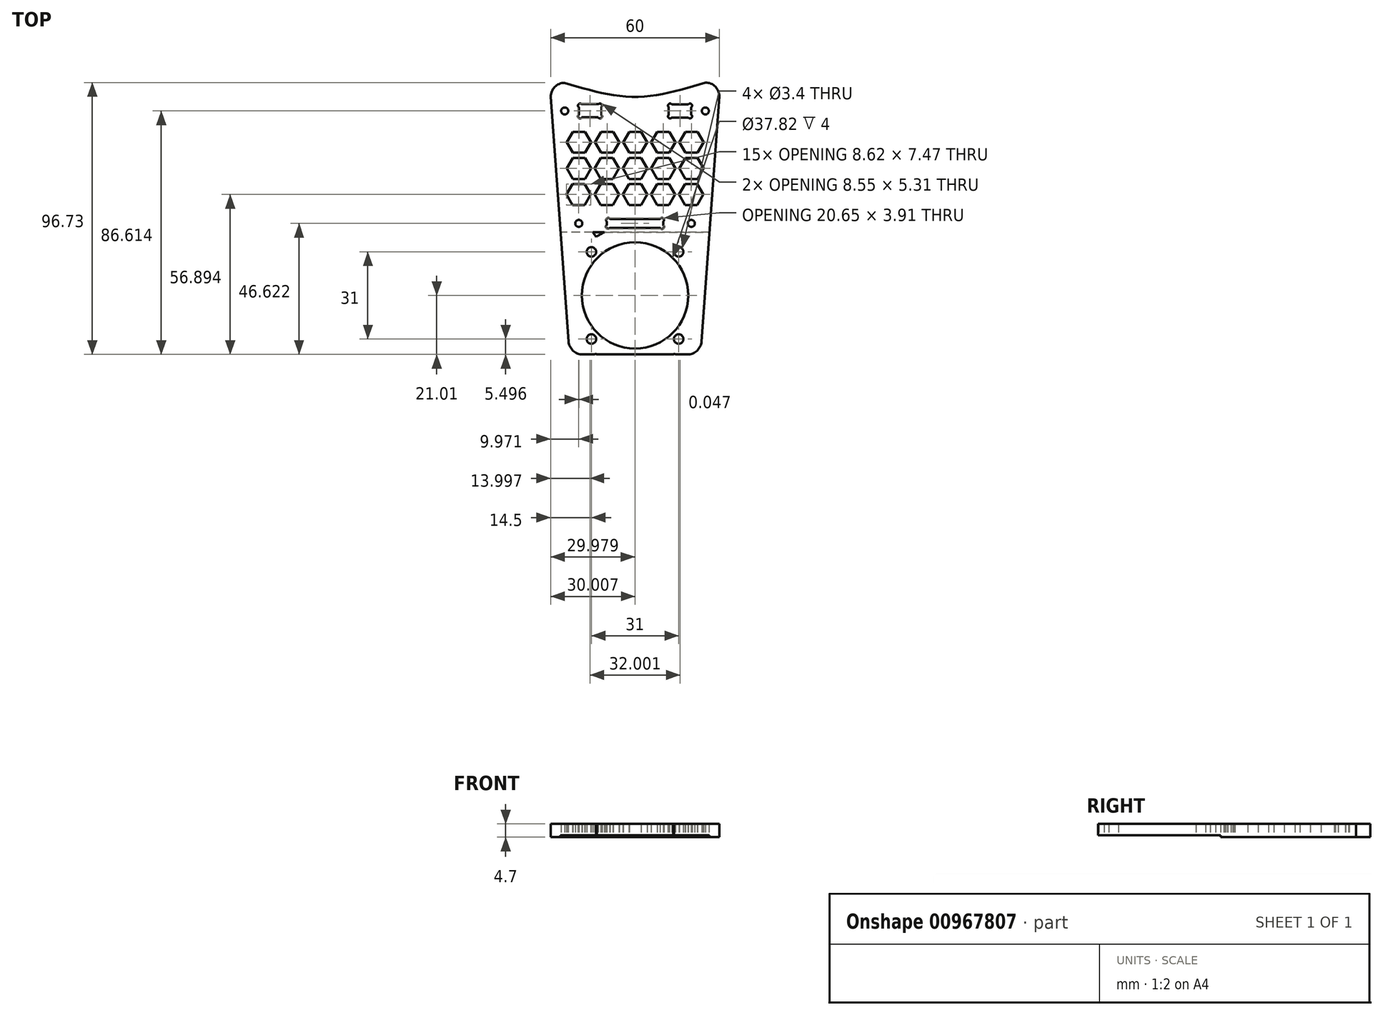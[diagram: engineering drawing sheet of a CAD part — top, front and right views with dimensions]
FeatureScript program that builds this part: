
annotation { "Feature Type Name" : "Feature", "Feature Type Description" : "" }
export const myFeature = defineFeature(function(context is Context, id is Id, definition is map)
    precondition{}
    {
        {
            var Q0;
            Q0=qCreatedBy(makeId("Top.planeOp"),FACE);
            var sketch = newSketch(context, id + "F0", { "sketchPlane" : qUnion([Q0])});
            skCircle(sketch, "E0", {"center": v(-24.72, 17.48) * mm, "radius": 1.25 * mm});
            skCircle(sketch, "E1", {"center": v(25.28, 17.48) * mm, "radius": 1.25 * mm});
            skLineSegment(sketch, "E2.bottom", {"start": v(20.28, 19.83) * mm, "end": v(12.28, 19.83) * mm});
            skLineSegment(sketch, "E2.top", {"start": v(20.28, 15.13) * mm, "end": v(12.28, 15.13) * mm});
            skLineSegment(sketch, "E2.left", {"start": v(20.28, 19.83) * mm, "end": v(20.28, 15.13) * mm});
            skLineSegment(sketch, "E2.right", {"start": v(12.28, 19.83) * mm, "end": v(12.28, 15.13) * mm});
            skPoint(sketch, "E3", {"position": v(0.28, -22.52) * mm});
            skLineSegment(sketch, "E4.bottom", {"start": v(-9.72, -20.9) * mm, "end": v(10.28, -20.9) * mm});
            skLineSegment(sketch, "E4.top", {"start": v(-9.72, -24.14) * mm, "end": v(10.28, -24.14) * mm});
            skLineSegment(sketch, "E4.left", {"start": v(-9.72, -20.9) * mm, "end": v(-9.72, -24.14) * mm});
            skLineSegment(sketch, "E4.right", {"start": v(10.28, -20.9) * mm, "end": v(10.28, -24.14) * mm});
            skCircle(sketch, "E5", {"center": v(20.28, -22.52) * mm, "radius": 1.25 * mm});
            skCircle(sketch, "E6", {"center": v(-19.72, -22.52) * mm, "radius": 1.25 * mm});
            skPoint(sketch, "E7.visualSharp", {"position": v(-29.72, 27.48) * mm});
            skArc(sketch, "E7.filletArc", {"start": v(-24.72, 27.48) * mm, "mid": v(-28.26, 26.02) * mm, "end": v(-29.72, 22.48) * mm});
            skPoint(sketch, "E8.visualSharp", {"position": v(30.28, 27.48) * mm});
            skArc(sketch, "E8.filletArc", {"start": v(30.28, 22.59) * mm, "mid": v(28.82, 26.12) * mm, "end": v(25.28, 27.59) * mm});
            skCircle(sketch, "E9", {"center": v(19.8, 15.57) * mm, "radius": 0.75 * mm});
            skCircle(sketch, "E10", {"center": v(12.75, 15.57) * mm, "radius": 0.75 * mm});
            skCircle(sketch, "E11", {"center": v(12.75, 19.38) * mm, "radius": 0.75 * mm});
            skCircle(sketch, "E12", {"center": v(19.8, 19.38) * mm, "radius": 0.75 * mm});
            skLineSegment(sketch, "E13.bottom", {"start": v(-11.72, 19.88) * mm, "end": v(-19.72, 19.88) * mm});
            skLineSegment(sketch, "E13.top", {"start": v(-11.72, 15.18) * mm, "end": v(-19.72, 15.18) * mm});
            skLineSegment(sketch, "E13.left", {"start": v(-11.72, 19.88) * mm, "end": v(-11.72, 15.18) * mm});
            skLineSegment(sketch, "E13.right", {"start": v(-19.72, 19.88) * mm, "end": v(-19.72, 15.18) * mm});
            skCircle(sketch, "E14", {"center": v(-12.2, 15.56) * mm, "radius": 0.75 * mm});
            skCircle(sketch, "E15", {"center": v(-19.25, 15.56) * mm, "radius": 0.75 * mm});
            skCircle(sketch, "E16", {"center": v(-19.25, 19.38) * mm, "radius": 0.75 * mm});
            skCircle(sketch, "E17", {"center": v(-12.2, 19.38) * mm, "radius": 0.75 * mm});
            skCircle(sketch, "E18", {"center": v(9.82, -21.3) * mm, "radius": 0.75 * mm});
            skCircle(sketch, "E19", {"center": v(-9.25, -21.33) * mm, "radius": 0.75 * mm});
            skCircle(sketch, "E20", {"center": v(-9.32, -23.66) * mm, "radius": 0.75 * mm});
            skCircle(sketch, "E21", {"center": v(9.83, -23.73) * mm, "radius": 0.75 * mm});
            skFitSpline(sketch, "E22", {"points": [v(-24.72, 27.48) * mm, v(0.28, 22.48) * mm, v(25.28, 27.59) * mm], "startDerivative": vector(50, -15) * mm, "endDerivative": vector(50, 15) * mm});
            skPoint(sketch, "E23", {"position": v(28, -0.27) * mm});
            skPoint(sketch, "E24.startSnap0", {"position": v(-15.72, 15.18) * mm});
            skPoint(sketch, "E25", {"position": v(-24.72, -45.86) * mm});
            skPoint(sketch, "E26", {"position": v(25.28, -45.72) * mm});
            skPoint(sketch, "E27.newPointB", {"position": v(25.28, -45.5) * mm});
            skPoint(sketch, "E28.newPointA", {"position": v(26.62, -27.41) * mm});
            skCircle(sketch, "E29.cCircle", {"center": v(20.25, -12.25) * mm, "radius": 3.73 * mm, "construction": true});
            skLineSegment(sketch, "E29.0", {"start": v(24.56, -12.25) * mm, "end": v(22.4, -15.98) * mm});
            skLineSegment(sketch, "E29.1", {"start": v(22.4, -15.98) * mm, "end": v(18.1, -15.98) * mm});
            skLineSegment(sketch, "E29.2", {"start": v(18.1, -15.98) * mm, "end": v(15.94, -12.25) * mm});
            skLineSegment(sketch, "E29.3", {"start": v(15.94, -12.25) * mm, "end": v(18.1, -8.51) * mm});
            skLineSegment(sketch, "E29.4", {"start": v(18.1, -8.51) * mm, "end": v(22.4, -8.51) * mm});
            skLineSegment(sketch, "E29.5", {"start": v(22.4, -8.51) * mm, "end": v(24.56, -12.25) * mm});
            skPoint(sketch, "E29.0.midPoint", {"position": v(23.48, -14.11) * mm});
            skLineSegment(sketch, "E30.1.0.0", {"start": v(12.4, -8.51) * mm, "end": v(14.56, -12.25) * mm});
            skCircle(sketch, "E30.1.0.1", {"center": v(10.25, -12.25) * mm, "radius": 3.73 * mm, "construction": true});
            skLineSegment(sketch, "E30.1.0.2", {"start": v(8.1, -15.98) * mm, "end": v(5.94, -12.25) * mm});
            skLineSegment(sketch, "E30.1.0.3", {"start": v(12.4, -15.98) * mm, "end": v(8.1, -15.98) * mm});
            skPoint(sketch, "E30.1.0.4", {"position": v(13.48, -14.11) * mm});
            skLineSegment(sketch, "E30.1.0.5", {"start": v(5.94, -12.25) * mm, "end": v(8.1, -8.51) * mm});
            skLineSegment(sketch, "E30.1.0.6", {"start": v(8.1, -8.51) * mm, "end": v(12.4, -8.51) * mm});
            skLineSegment(sketch, "E30.1.0.7", {"start": v(14.56, -12.25) * mm, "end": v(12.4, -15.98) * mm});
            skLineSegment(sketch, "E30.direction1", {"start": v(18.1, -15.98) * mm, "end": v(8.1, -15.98) * mm, "construction": true});
            skLineSegment(sketch, "E30.direction2", {"start": v(18.1, -15.98) * mm, "end": v(18.14, -6.68) * mm, "construction": true});
            skCircle(sketch, "E31", {"center": v(0.28, -48.14) * mm, "radius": 12 * mm});
            skLineSegment(sketch, "E32", {"start": v(-18.37, -69.14) * mm, "end": v(18.92, -69.14) * mm});
            skPoint(sketch, "E33.visualSharp", {"position": v(-23.01, -69.14) * mm});
            skArc(sketch, "E33.filletArc", {"start": v(-23.35, -64.5) * mm, "mid": v(-21.77, -67.8) * mm, "end": v(-18.37, -69.14) * mm});
            skPoint(sketch, "E34.visualSharp", {"position": v(23.56, -69.14) * mm});
            skArc(sketch, "E34.filletArc", {"start": v(18.92, -69.14) * mm, "mid": v(22.32, -67.8) * mm, "end": v(23.9, -64.5) * mm});
            skCircle(sketch, "E35", {"center": v(15.78, -32.64) * mm, "radius": 1.7 * mm});
            skCircle(sketch, "E36", {"center": v(-15.22, -32.64) * mm, "radius": 1.7 * mm});
            skCircle(sketch, "E37", {"center": v(-15.22, -63.64) * mm, "radius": 1.7 * mm});
            skCircle(sketch, "E38", {"center": v(15.78, -63.64) * mm, "radius": 1.7 * mm});
            skLineSegment(sketch, "E39.0.2.0", {"start": v(2.4, -8.51) * mm, "end": v(4.56, -12.25) * mm});
            skCircle(sketch, "E39.3.2.0", {"center": v(0.25, -12.25) * mm, "radius": 3.73 * mm, "construction": true});
            skLineSegment(sketch, "E39.5.2.0", {"start": v(-1.9, -15.98) * mm, "end": v(-4.06, -12.25) * mm});
            skLineSegment(sketch, "E39.8.2.0", {"start": v(2.4, -15.98) * mm, "end": v(-1.9, -15.98) * mm});
            skPoint(sketch, "E39.11.2.0", {"position": v(3.48, -14.11) * mm});
            skLineSegment(sketch, "E39.12.2.0", {"start": v(-4.06, -12.25) * mm, "end": v(-1.9, -8.51) * mm});
            skLineSegment(sketch, "E39.15.2.0", {"start": v(-1.9, -8.51) * mm, "end": v(2.4, -8.51) * mm});
            skLineSegment(sketch, "E39.18.2.0", {"start": v(4.56, -12.25) * mm, "end": v(2.4, -15.98) * mm});
            skLineSegment(sketch, "E39.0.3.0", {"start": v(-7.6, -8.51) * mm, "end": v(-5.44, -12.25) * mm});
            skCircle(sketch, "E39.3.3.0", {"center": v(-9.75, -12.25) * mm, "radius": 3.73 * mm, "construction": true});
            skLineSegment(sketch, "E39.5.3.0", {"start": v(-11.9, -15.98) * mm, "end": v(-14.06, -12.25) * mm});
            skLineSegment(sketch, "E39.8.3.0", {"start": v(-7.6, -15.98) * mm, "end": v(-11.9, -15.98) * mm});
            skPoint(sketch, "E39.11.3.0", {"position": v(-6.52, -14.11) * mm});
            skLineSegment(sketch, "E39.12.3.0", {"start": v(-14.06, -12.25) * mm, "end": v(-11.9, -8.51) * mm});
            skLineSegment(sketch, "E39.15.3.0", {"start": v(-11.9, -8.51) * mm, "end": v(-7.6, -8.51) * mm});
            skLineSegment(sketch, "E39.18.3.0", {"start": v(-5.44, -12.25) * mm, "end": v(-7.6, -15.98) * mm});
            skLineSegment(sketch, "E40.0.0.1", {"start": v(22.45, 0.78) * mm, "end": v(24.6, -2.95) * mm});
            skCircle(sketch, "E40.3.0.1", {"center": v(20.3, -2.95) * mm, "radius": 3.73 * mm, "construction": true});
            skLineSegment(sketch, "E40.5.0.1", {"start": v(18.14, -6.68) * mm, "end": v(15.99, -2.95) * mm});
            skLineSegment(sketch, "E40.8.0.1", {"start": v(22.45, -6.68) * mm, "end": v(18.14, -6.68) * mm});
            skPoint(sketch, "E40.11.0.1", {"position": v(23.53, -4.82) * mm});
            skLineSegment(sketch, "E40.12.0.1", {"start": v(15.99, -2.95) * mm, "end": v(18.14, 0.78) * mm});
            skLineSegment(sketch, "E40.15.0.1", {"start": v(18.14, 0.78) * mm, "end": v(22.45, 0.78) * mm});
            skLineSegment(sketch, "E40.18.0.1", {"start": v(24.6, -2.95) * mm, "end": v(22.45, -6.68) * mm});
            skLineSegment(sketch, "E40.0.0.2", {"start": v(22.5, 10.07) * mm, "end": v(24.66, 6.34) * mm});
            skCircle(sketch, "E40.3.0.2", {"center": v(20.34, 6.34) * mm, "radius": 3.73 * mm, "construction": true});
            skLineSegment(sketch, "E40.5.0.2", {"start": v(18.19, 2.6) * mm, "end": v(16.03, 6.34) * mm});
            skLineSegment(sketch, "E40.8.0.2", {"start": v(22.5, 2.6) * mm, "end": v(18.19, 2.6) * mm});
            skPoint(sketch, "E40.11.0.2", {"position": v(23.58, 4.48) * mm});
            skLineSegment(sketch, "E40.12.0.2", {"start": v(16.03, 6.34) * mm, "end": v(18.19, 10.07) * mm});
            skLineSegment(sketch, "E40.15.0.2", {"start": v(18.19, 10.07) * mm, "end": v(22.5, 10.07) * mm});
            skLineSegment(sketch, "E40.18.0.2", {"start": v(24.66, 6.34) * mm, "end": v(22.5, 2.6) * mm});
            skLineSegment(sketch, "E40.0.1.1", {"start": v(12.45, 0.78) * mm, "end": v(14.6, -2.95) * mm});
            skCircle(sketch, "E40.3.1.1", {"center": v(10.3, -2.95) * mm, "radius": 3.73 * mm, "construction": true});
            skLineSegment(sketch, "E40.5.1.1", {"start": v(8.14, -6.68) * mm, "end": v(5.99, -2.95) * mm});
            skLineSegment(sketch, "E40.8.1.1", {"start": v(12.45, -6.68) * mm, "end": v(8.14, -6.68) * mm});
            skPoint(sketch, "E40.11.1.1", {"position": v(13.53, -4.82) * mm});
            skLineSegment(sketch, "E40.12.1.1", {"start": v(5.99, -2.95) * mm, "end": v(8.14, 0.78) * mm});
            skLineSegment(sketch, "E40.15.1.1", {"start": v(8.14, 0.78) * mm, "end": v(12.45, 0.78) * mm});
            skLineSegment(sketch, "E40.18.1.1", {"start": v(14.6, -2.95) * mm, "end": v(12.45, -6.68) * mm});
            skLineSegment(sketch, "E40.0.1.2", {"start": v(12.5, 10.07) * mm, "end": v(14.66, 6.34) * mm});
            skCircle(sketch, "E40.3.1.2", {"center": v(10.34, 6.34) * mm, "radius": 3.73 * mm, "construction": true});
            skLineSegment(sketch, "E40.5.1.2", {"start": v(8.19, 2.6) * mm, "end": v(6.03, 6.34) * mm});
            skLineSegment(sketch, "E40.8.1.2", {"start": v(12.5, 2.6) * mm, "end": v(8.19, 2.6) * mm});
            skPoint(sketch, "E40.11.1.2", {"position": v(13.58, 4.48) * mm});
            skLineSegment(sketch, "E40.12.1.2", {"start": v(6.03, 6.34) * mm, "end": v(8.19, 10.07) * mm});
            skLineSegment(sketch, "E40.15.1.2", {"start": v(8.19, 10.07) * mm, "end": v(12.5, 10.07) * mm});
            skLineSegment(sketch, "E40.18.1.2", {"start": v(14.66, 6.34) * mm, "end": v(12.5, 2.6) * mm});
            skLineSegment(sketch, "E40.0.2.1", {"start": v(2.45, 0.78) * mm, "end": v(4.6, -2.95) * mm});
            skCircle(sketch, "E40.3.2.1", {"center": v(0.3, -2.95) * mm, "radius": 3.73 * mm, "construction": true});
            skLineSegment(sketch, "E40.5.2.1", {"start": v(-1.86, -6.68) * mm, "end": v(-4.01, -2.95) * mm});
            skLineSegment(sketch, "E40.8.2.1", {"start": v(2.45, -6.68) * mm, "end": v(-1.86, -6.68) * mm});
            skPoint(sketch, "E40.11.2.1", {"position": v(3.53, -4.82) * mm});
            skLineSegment(sketch, "E40.12.2.1", {"start": v(-4.01, -2.95) * mm, "end": v(-1.86, 0.78) * mm});
            skLineSegment(sketch, "E40.15.2.1", {"start": v(-1.86, 0.78) * mm, "end": v(2.45, 0.78) * mm});
            skLineSegment(sketch, "E40.18.2.1", {"start": v(4.6, -2.95) * mm, "end": v(2.45, -6.68) * mm});
            skLineSegment(sketch, "E40.0.2.2", {"start": v(2.5, 10.07) * mm, "end": v(4.66, 6.34) * mm});
            skCircle(sketch, "E40.3.2.2", {"center": v(0.34, 6.34) * mm, "radius": 3.73 * mm, "construction": true});
            skLineSegment(sketch, "E40.5.2.2", {"start": v(-1.81, 2.6) * mm, "end": v(-3.97, 6.34) * mm});
            skLineSegment(sketch, "E40.8.2.2", {"start": v(2.5, 2.6) * mm, "end": v(-1.81, 2.6) * mm});
            skPoint(sketch, "E40.11.2.2", {"position": v(3.58, 4.48) * mm});
            skLineSegment(sketch, "E40.12.2.2", {"start": v(-3.97, 6.34) * mm, "end": v(-1.81, 10.07) * mm});
            skLineSegment(sketch, "E40.15.2.2", {"start": v(-1.81, 10.07) * mm, "end": v(2.5, 10.07) * mm});
            skLineSegment(sketch, "E40.18.2.2", {"start": v(4.66, 6.34) * mm, "end": v(2.5, 2.6) * mm});
            skLineSegment(sketch, "E40.0.3.1", {"start": v(-7.55, 0.78) * mm, "end": v(-5.4, -2.95) * mm});
            skCircle(sketch, "E40.3.3.1", {"center": v(-9.7, -2.95) * mm, "radius": 3.73 * mm, "construction": true});
            skLineSegment(sketch, "E40.5.3.1", {"start": v(-11.86, -6.68) * mm, "end": v(-14.01, -2.95) * mm});
            skLineSegment(sketch, "E40.8.3.1", {"start": v(-7.55, -6.68) * mm, "end": v(-11.86, -6.68) * mm});
            skPoint(sketch, "E40.11.3.1", {"position": v(-6.47, -4.82) * mm});
            skLineSegment(sketch, "E40.12.3.1", {"start": v(-14.01, -2.95) * mm, "end": v(-11.86, 0.78) * mm});
            skLineSegment(sketch, "E40.15.3.1", {"start": v(-11.86, 0.78) * mm, "end": v(-7.55, 0.78) * mm});
            skLineSegment(sketch, "E40.18.3.1", {"start": v(-5.4, -2.95) * mm, "end": v(-7.55, -6.68) * mm});
            skLineSegment(sketch, "E40.0.3.2", {"start": v(-7.5, 10.07) * mm, "end": v(-5.34, 6.34) * mm});
            skCircle(sketch, "E40.3.3.2", {"center": v(-9.66, 6.34) * mm, "radius": 3.73 * mm, "construction": true});
            skLineSegment(sketch, "E40.5.3.2", {"start": v(-11.81, 2.6) * mm, "end": v(-13.97, 6.34) * mm});
            skLineSegment(sketch, "E40.8.3.2", {"start": v(-7.5, 2.6) * mm, "end": v(-11.81, 2.6) * mm});
            skPoint(sketch, "E40.11.3.2", {"position": v(-6.42, 4.48) * mm});
            skLineSegment(sketch, "E40.12.3.2", {"start": v(-13.97, 6.34) * mm, "end": v(-11.81, 10.07) * mm});
            skLineSegment(sketch, "E40.15.3.2", {"start": v(-11.81, 10.07) * mm, "end": v(-7.5, 10.07) * mm});
            skLineSegment(sketch, "E40.18.3.2", {"start": v(-5.34, 6.34) * mm, "end": v(-7.5, 2.6) * mm});
            skLineSegment(sketch, "E41.0.4.0", {"start": v(-17.6, -8.51) * mm, "end": v(-15.44, -12.25) * mm});
            skCircle(sketch, "E41.3.4.0", {"center": v(-19.75, -12.25) * mm, "radius": 3.73 * mm, "construction": true});
            skLineSegment(sketch, "E41.5.4.0", {"start": v(-21.9, -15.98) * mm, "end": v(-24.06, -12.25) * mm});
            skLineSegment(sketch, "E41.8.4.0", {"start": v(-17.6, -15.98) * mm, "end": v(-21.9, -15.98) * mm});
            skPoint(sketch, "E41.11.4.0", {"position": v(-16.52, -14.11) * mm});
            skLineSegment(sketch, "E41.12.4.0", {"start": v(-24.06, -12.25) * mm, "end": v(-21.9, -8.51) * mm});
            skLineSegment(sketch, "E41.15.4.0", {"start": v(-21.9, -8.51) * mm, "end": v(-17.6, -8.51) * mm});
            skLineSegment(sketch, "E41.18.4.0", {"start": v(-15.44, -12.25) * mm, "end": v(-17.6, -15.98) * mm});
            skLineSegment(sketch, "E41.0.4.1", {"start": v(-17.55, 0.78) * mm, "end": v(-15.4, -2.95) * mm});
            skCircle(sketch, "E41.3.4.1", {"center": v(-19.7, -2.95) * mm, "radius": 3.73 * mm, "construction": true});
            skLineSegment(sketch, "E41.5.4.1", {"start": v(-21.86, -6.68) * mm, "end": v(-24.01, -2.95) * mm});
            skLineSegment(sketch, "E41.8.4.1", {"start": v(-17.55, -6.68) * mm, "end": v(-21.86, -6.68) * mm});
            skPoint(sketch, "E41.11.4.1", {"position": v(-16.47, -4.82) * mm});
            skLineSegment(sketch, "E41.12.4.1", {"start": v(-24.01, -2.95) * mm, "end": v(-21.86, 0.78) * mm});
            skLineSegment(sketch, "E41.15.4.1", {"start": v(-21.86, 0.78) * mm, "end": v(-17.55, 0.78) * mm});
            skLineSegment(sketch, "E41.18.4.1", {"start": v(-15.4, -2.95) * mm, "end": v(-17.55, -6.68) * mm});
            skLineSegment(sketch, "E41.0.4.2", {"start": v(-17.5, 10.07) * mm, "end": v(-15.34, 6.34) * mm});
            skCircle(sketch, "E41.3.4.2", {"center": v(-19.66, 6.34) * mm, "radius": 3.73 * mm, "construction": true});
            skLineSegment(sketch, "E41.5.4.2", {"start": v(-21.81, 2.6) * mm, "end": v(-23.97, 6.34) * mm});
            skLineSegment(sketch, "E41.8.4.2", {"start": v(-17.5, 2.6) * mm, "end": v(-21.81, 2.6) * mm});
            skPoint(sketch, "E41.11.4.2", {"position": v(-16.42, 4.48) * mm});
            skLineSegment(sketch, "E41.12.4.2", {"start": v(-23.97, 6.34) * mm, "end": v(-21.81, 10.07) * mm});
            skLineSegment(sketch, "E41.15.4.2", {"start": v(-21.81, 10.07) * mm, "end": v(-17.5, 10.07) * mm});
            skLineSegment(sketch, "E41.18.4.2", {"start": v(-15.34, 6.34) * mm, "end": v(-17.5, 2.6) * mm});
            skLineSegment(sketch, "E42", {"start": v(0.28, -20.9) * mm, "end": v(0.28, 15.18) * mm});
            skPoint(sketch, "E43", {"position": v(0.28, -2.86) * mm});
            skCircle(sketch, "E44.cCircle", {"center": v(0.29, -48.13) * mm, "radius": 27.62 * mm, "construction": true});
            skLineSegment(sketch, "E44.0", {"start": v(27.9, -42.64) * mm, "end": v(27.9, -53.62) * mm});
            skLineSegment(sketch, "E44.1", {"start": v(27.9, -53.62) * mm, "end": v(23.7, -63.77) * mm});
            skLineSegment(sketch, "E44.2", {"start": v(23.7, -63.77) * mm, "end": v(15.93, -71.54) * mm});
            skLineSegment(sketch, "E44.3", {"start": v(15.93, -71.54) * mm, "end": v(5.78, -75.75) * mm});
            skLineSegment(sketch, "E44.4", {"start": v(5.78, -75.75) * mm, "end": v(-5.2, -75.75) * mm});
            skLineSegment(sketch, "E44.5", {"start": v(-5.2, -75.75) * mm, "end": v(-15.36, -71.54) * mm});
            skLineSegment(sketch, "E44.6", {"start": v(-15.36, -71.54) * mm, "end": v(-23.13, -63.77) * mm});
            skLineSegment(sketch, "E44.7", {"start": v(-23.13, -63.77) * mm, "end": v(-27.33, -53.62) * mm});
            skLineSegment(sketch, "E44.8", {"start": v(-27.33, -53.62) * mm, "end": v(-27.33, -42.64) * mm});
            skLineSegment(sketch, "E44.9", {"start": v(-27.33, -42.64) * mm, "end": v(-23.13, -32.49) * mm});
            skLineSegment(sketch, "E44.10", {"start": v(-23.13, -32.49) * mm, "end": v(-15.36, -24.72) * mm});
            skLineSegment(sketch, "E44.11", {"start": v(-15.36, -24.72) * mm, "end": v(-5.2, -20.51) * mm});
            skLineSegment(sketch, "E44.12", {"start": v(-5.2, -20.51) * mm, "end": v(5.78, -20.51) * mm});
            skLineSegment(sketch, "E44.13", {"start": v(5.78, -20.51) * mm, "end": v(15.93, -24.72) * mm});
            skLineSegment(sketch, "E44.14", {"start": v(15.93, -24.72) * mm, "end": v(23.7, -32.49) * mm});
            skLineSegment(sketch, "E44.15", {"start": v(23.7, -32.49) * mm, "end": v(27.9, -42.64) * mm});
            skPoint(sketch, "E44.0.midPoint", {"position": v(27.9, -48.13) * mm});
            skCircle(sketch, "E45", {"center": v(0.28, -48.14) * mm, "radius": 15 * mm});
            skCircle(sketch, "E46", {"center": v(0.29, -48.13) * mm, "radius": 25 * mm});
            skLineSegment(sketch, "E47", {"start": v(0.29, -48.13) * mm, "end": v(15.93, -24.72) * mm});
            skLineSegment(sketch, "E48", {"start": v(0.29, -48.13) * mm, "end": v(23.7, -32.49) * mm});
            skLineSegment(sketch, "E49", {"start": v(0.29, -48.13) * mm, "end": v(-15.36, -24.72) * mm});
            skLineSegment(sketch, "E50", {"start": v(0.29, -48.13) * mm, "end": v(-23.13, -32.49) * mm});
            skLineSegment(sketch, "E51", {"start": v(0.29, -48.13) * mm, "end": v(-15.36, -71.54) * mm});
            skLineSegment(sketch, "E52", {"start": v(0.29, -48.13) * mm, "end": v(-23.13, -63.77) * mm});
            skLineSegment(sketch, "E53", {"start": v(0.29, -48.13) * mm, "end": v(15.93, -71.54) * mm});
            skLineSegment(sketch, "E54", {"start": v(0.29, -48.13) * mm, "end": v(23.7, -63.77) * mm});
            skCircle(sketch, "E55", {"center": v(0.29, -48.13) * mm, "radius": 18.91 * mm});
            skCircle(sketch, "E56", {"center": v(0.29, -48.13) * mm, "radius": 21.85 * mm});
            skLineSegment(sketch, "E57", {"start": v(0.28, -24.14) * mm, "end": v(0.28, -25.64) * mm});
            skLineSegment(sketch, "E58", {"start": v(0.28, -25.64) * mm, "end": v(-26.2, -25.64) * mm});
            skLineSegment(sketch, "E59", {"start": v(0.28, -25.64) * mm, "end": v(26.75, -25.64) * mm});
            skLineSegment(sketch, "E60.bottom", {"start": v(-26.2, -25.64) * mm, "end": v(26.75, -25.64) * mm});
            skLineSegment(sketch, "E60.top", {"start": v(-26.2, -70.75) * mm, "end": v(26.75, -70.75) * mm});
            skLineSegment(sketch, "E60.left", {"start": v(-26.2, -25.64) * mm, "end": v(-26.2, -70.75) * mm});
            skLineSegment(sketch, "E60.right", {"start": v(26.75, -25.64) * mm, "end": v(26.75, -70.75) * mm});
            skLineSegment(sketch, "E61", {"start": v(-29.72, 22.48) * mm, "end": v(-23.35, -64.5) * mm});
            skLineSegment(sketch, "E62", {"start": v(30.28, 22.59) * mm, "end": v(23.9, -64.5) * mm});
            skSolve(sketch);
        }
        {
            var Q0;
            Q0=makeQuery(id+"F0.imprint","IMPRINT",FACE,{"disambiguationData":[TD([[makeQuery(id+"F0.imprint","IMPRINT",EDGE,{"derivedFrom":sQuery(id+"F0.wireOp",EDGE,"E0")}),-1.0]])]});
            var Q1;
            Q1=makeQuery(id+"F0.imprint","IMPRINT",FACE,{"disambiguationData":[TD([[makeQuery(id+"F0.imprint","IMPRINT",EDGE,{"derivedFrom":sQuery(id+"F0.wireOp",EDGE,"AtNKITw1-TZqG-d9z5-eSek-5ZgDB1EEJ3aK")}),-1.0]])]});
            var Q2;
            {var subQ0=sQuery(id+"F0.wireOp",EDGE,"E20");var subQ1=sQuery(id+"F0.wireOp",EDGE,"E4.top");var subQ2=makeQuery(id+"F0.imprint","INTERSECT",VERTEX,{"derivedFrom":[subQ1,subQ0]});Q2=makeQuery(id+"F0.imprint","IMPRINT",FACE,{"disambiguationData":[TD([[makeQuery(id+"F0.imprint","IMPRINT",EDGE,{"disambiguationData":[TD([[subQ2,-1.0]])],"derivedFrom":subQ1}),-1.0]])]});}
            var Q3;
            {var subQ1=sQuery(id+"F0.wireOp",EDGE,"E46");var subQ5=sQuery(id+"F0.wireOp",EDGE,"E4.top");var subQ6=makeQuery(id+"F0.imprint","INTERSECT",VERTEX,{"disambiguationData":[OD(0.0)],"derivedFrom":[subQ5,subQ1]});Q3=makeQuery(id+"F0.imprint","IMPRINT",FACE,{"disambiguationData":[TD([[makeQuery(id+"F0.imprint","IMPRINT",EDGE,{"disambiguationData":[TD([[subQ6,-1.0]])],"derivedFrom":subQ5}),-1.0]])]});}
            var Q4;
            Q4=makeQuery(id+"F0.imprint","IMPRINT",FACE,{"disambiguationData":[TD([[makeQuery(id+"F0.imprint","IMPRINT",EDGE,{"derivedFrom":sQuery(id+"F0.wireOp",EDGE,"E35")}),-1.0]])]});
            var Q5;
            {var subQ7=sQuery(id+"F0.wireOp",EDGE,"E4.top");var subQ9=sQuery(id+"F0.wireOp",EDGE,"E46");var subQ10=makeQuery(id+"F0.imprint","INTERSECT",VERTEX,{"disambiguationData":[OD(1.0)],"derivedFrom":[subQ7,subQ9]});Q5=makeQuery(id+"F0.imprint","IMPRINT",FACE,{"disambiguationData":[TD([[makeQuery(id+"F0.imprint","IMPRINT",EDGE,{"disambiguationData":[TD([[subQ10,-1.0]])],"derivedFrom":subQ7}),-1.0]])]});}
            var Q6;
            {var subQ0=sQuery(id+"F0.wireOp",EDGE,"E44.14");Q6=makeQuery(id+"F0.imprint","IMPRINT",FACE,{"disambiguationData":[TD([[makeQuery(id+"F0.imprint","IMPRINT",EDGE,{"derivedFrom":subQ0}),-1.0]])]});}
            var Q7;
            {var subQ0=sQuery(id+"F0.wireOp",EDGE,"E44.10");Q7=makeQuery(id+"F0.imprint","IMPRINT",FACE,{"disambiguationData":[TD([[makeQuery(id+"F0.imprint","IMPRINT",EDGE,{"derivedFrom":subQ0}),-1.0]])]});}
            var Q8;
            Q8=makeQuery(id+"F0.imprint","IMPRINT",FACE,{"disambiguationData":[TD([[makeQuery(id+"F0.imprint","IMPRINT",EDGE,{"derivedFrom":sQuery(id+"F0.wireOp",EDGE,"E36")}),-1.0]])]});
            var Q9;
            {var subQ0=sQuery(id+"F0.wireOp",EDGE,"E44.15");var subQ1=sQuery(id+"F0.wireOp",EDGE,"Fv1uCipX-vUk0-Yfkj-1D7Z-x97Jl5sTBQmt");var subQ2=makeQuery(id+"F0.imprint","INTERSECT",VERTEX,{"derivedFrom":[subQ1,subQ0]});Q9=makeQuery(id+"F0.imprint","IMPRINT",FACE,{"disambiguationData":[TD([[makeQuery(id+"F0.imprint","IMPRINT",EDGE,{"disambiguationData":[TD([[subQ2,-1.0]])],"derivedFrom":subQ1}),-1.0]])]});}
            var Q10;
            {var subQ0=sQuery(id+"F0.wireOp",EDGE,"E44.1");var subQ1=sQuery(id+"F0.wireOp",EDGE,"Fv1uCipX-vUk0-Yfkj-1D7Z-x97Jl5sTBQmt");var subQ2=makeQuery(id+"F0.imprint","INTERSECT",VERTEX,{"derivedFrom":[subQ1,subQ0]});Q10=makeQuery(id+"F0.imprint","IMPRINT",FACE,{"disambiguationData":[TD([[makeQuery(id+"F0.imprint","IMPRINT",EDGE,{"disambiguationData":[TD([[subQ2,1.0]])],"derivedFrom":subQ1}),-1.0]])]});}
            var Q11;
            {var subQ1=sQuery(id+"F0.wireOp",EDGE,"E46");var subQ5=sQuery(id+"F0.wireOp",EDGE,"Fv1uCipX-vUk0-Yfkj-1D7Z-x97Jl5sTBQmt");var subQ9=makeQuery(id+"F0.imprint","INTERSECT",VERTEX,{"disambiguationData":[OD(0.0)],"derivedFrom":[subQ5,subQ1]});Q11=makeQuery(id+"F0.imprint","IMPRINT",FACE,{"disambiguationData":[TD([[makeQuery(id+"F0.imprint","IMPRINT",EDGE,{"disambiguationData":[TD([[subQ9,-1.0]])],"derivedFrom":subQ5}),-1.0]])]});}
            var Q12;
            Q12=makeQuery(id+"F0.imprint","IMPRINT",FACE,{"disambiguationData":[TD([[makeQuery(id+"F0.imprint","IMPRINT",EDGE,{"derivedFrom":sQuery(id+"F0.wireOp",EDGE,"E37")}),-1.0]])]});
            var Q13;
            {var subQ1=sQuery(id+"F0.wireOp",EDGE,"E46");var subQ8=sQuery(id+"F0.wireOp",EDGE,"CWTrbjSd-p9ir-Zju1-9z6i-MnSNEF0wIDjJ");var subQ10=makeQuery(id+"F0.imprint","INTERSECT",VERTEX,{"disambiguationData":[OD(0.0)],"derivedFrom":[subQ8,subQ1]});Q13=makeQuery(id+"F0.imprint","IMPRINT",FACE,{"disambiguationData":[TD([[makeQuery(id+"F0.imprint","IMPRINT",EDGE,{"disambiguationData":[TD([[subQ10,-1.0]])],"derivedFrom":subQ8}),1.0]])]});}
            var Q14;
            {var subQ1=sQuery(id+"F0.wireOp",EDGE,"CWTrbjSd-p9ir-Zju1-9z6i-MnSNEF0wIDjJ");var subQ5=makeQuery(id+"F0.imprint","IMPRINT",VERTEX,{"derivedFrom":subQ1});Q14=makeQuery(id+"F0.imprint","IMPRINT",FACE,{"disambiguationData":[TD([[makeQuery(id+"F0.imprint","IMPRINT",EDGE,{"disambiguationData":[TD([[subQ5,1.0]])],"derivedFrom":subQ1}),1.0]])]});}
            var Q15;
            {var subQ0=sQuery(id+"F0.wireOp",EDGE,"E44.7");var subQ1=sQuery(id+"F0.wireOp",EDGE,"CWTrbjSd-p9ir-Zju1-9z6i-MnSNEF0wIDjJ");var subQ2=makeQuery(id+"F0.imprint","INTERSECT",VERTEX,{"derivedFrom":[subQ1,subQ0]});Q15=makeQuery(id+"F0.imprint","IMPRINT",FACE,{"disambiguationData":[TD([[makeQuery(id+"F0.imprint","IMPRINT",EDGE,{"disambiguationData":[TD([[subQ2,1.0]])],"derivedFrom":subQ1}),1.0]])]});}
            var Q16;
            {var subQ5=sQuery(id+"F0.wireOp",EDGE,"E44.6");var subQ7=sQuery(id+"F0.wireOp",EDGE,"E32");var subQ8=makeQuery(id+"F0.imprint","INTERSECT",VERTEX,{"derivedFrom":[subQ7,subQ5]});Q16=makeQuery(id+"F0.imprint","IMPRINT",FACE,{"disambiguationData":[TD([[makeQuery(id+"F0.imprint","IMPRINT",EDGE,{"disambiguationData":[TD([[subQ8,-1.0]])],"derivedFrom":subQ7}),1.0]])]});}
            var Q17;
            {var subQ0=sQuery(id+"F0.wireOp",EDGE,"E33.filletArc");Q17=makeQuery(id+"F0.imprint","IMPRINT",FACE,{"disambiguationData":[TD([[makeQuery(id+"F0.imprint","IMPRINT",EDGE,{"derivedFrom":subQ0}),1.0]])]});}
            var Q18;
            Q18=makeQuery(id+"F0.imprint","IMPRINT",FACE,{"disambiguationData":[TD([[makeQuery(id+"F0.imprint","IMPRINT",EDGE,{"derivedFrom":sQuery(id+"F0.wireOp",EDGE,"E38")}),-1.0]])]});
            var Q19;
            {var subQ1=sQuery(id+"F0.wireOp",EDGE,"E32");var subQ7=sQuery(id+"F0.wireOp",EDGE,"E44.2");var subQ9=makeQuery(id+"F0.imprint","INTERSECT",VERTEX,{"derivedFrom":[subQ1,subQ7]});Q19=makeQuery(id+"F0.imprint","IMPRINT",FACE,{"disambiguationData":[TD([[makeQuery(id+"F0.imprint","IMPRINT",EDGE,{"disambiguationData":[TD([[subQ9,1.0]])],"derivedFrom":subQ1}),1.0]])]});}
            var Q20;
            {var subQ5=sQuery(id+"F0.wireOp",EDGE,"E34.filletArc");Q20=makeQuery(id+"F0.imprint","IMPRINT",FACE,{"disambiguationData":[TD([[makeQuery(id+"F0.imprint","IMPRINT",EDGE,{"derivedFrom":subQ5}),1.0]])]});}
            var Q21;
            {var subQ1=sQuery(id+"F0.wireOp",EDGE,"CWTrbjSd-p9ir-Zju1-9z6i-MnSNEF0wIDjJ");var subQ3=sQuery(id+"F0.wireOp",EDGE,"E44.9");var subQ4=makeQuery(id+"F0.imprint","INTERSECT",VERTEX,{"derivedFrom":[subQ1,subQ3]});Q21=makeQuery(id+"F0.imprint","IMPRINT",FACE,{"disambiguationData":[TD([[makeQuery(id+"F0.imprint","IMPRINT",EDGE,{"disambiguationData":[TD([[subQ4,1.0]])],"derivedFrom":subQ1}),1.0]])]});}
            var Q22;
            {var subQ3=sQuery(id+"F0.wireOp",EDGE,"E46");var subQ5=sQuery(id+"F0.wireOp",EDGE,"E49");var subQ6=makeQuery(id+"F0.imprint","INTERSECT",VERTEX,{"derivedFrom":[subQ3,subQ5]});Q22=makeQuery(id+"F0.imprint","IMPRINT",FACE,{"disambiguationData":[TD([[makeQuery(id+"F0.imprint","IMPRINT",EDGE,{"disambiguationData":[TD([[subQ6,-1.0]])],"derivedFrom":subQ3}),-1.0]])]});}
            var Q23;
            {var subQ0=sQuery(id+"F0.wireOp",EDGE,"E60.bottom");var subQ1=sQuery(id+"F0.wireOp",EDGE,"E46");var subQ2=makeQuery(id+"F0.imprint","INTERSECT",VERTEX,{"disambiguationData":[OD(1.0)],"derivedFrom":[subQ1,subQ0]});Q23=makeQuery(id+"F0.imprint","IMPRINT",FACE,{"disambiguationData":[TD([[makeQuery(id+"F0.imprint","IMPRINT",EDGE,{"disambiguationData":[TD([[subQ2,-1.0]])],"derivedFrom":subQ1}),-1.0]])]});}
            var Q24;
            {var subQ0=sQuery(id+"F0.wireOp",EDGE,"E57");Q24=makeQuery(id+"F0.imprint","IMPRINT",FACE,{"disambiguationData":[TD([[makeQuery(id+"F0.imprint","IMPRINT",EDGE,{"derivedFrom":subQ0}),1.0]])]});}
            var Q25;
            {var subQ0=sQuery(id+"F0.wireOp",EDGE,"E47");var subQ1=sQuery(id+"F0.wireOp",EDGE,"E46");var subQ2=makeQuery(id+"F0.imprint","INTERSECT",VERTEX,{"derivedFrom":[subQ1,subQ0]});Q25=makeQuery(id+"F0.imprint","IMPRINT",FACE,{"disambiguationData":[TD([[makeQuery(id+"F0.imprint","IMPRINT",EDGE,{"disambiguationData":[TD([[subQ2,-1.0]])],"derivedFrom":subQ1}),-1.0]])]});}
            var Q26;
            {var subQ1=sQuery(id+"F0.wireOp",EDGE,"Fv1uCipX-vUk0-Yfkj-1D7Z-x97Jl5sTBQmt");var subQ3=sQuery(id+"F0.wireOp",EDGE,"E44.15");var subQ4=makeQuery(id+"F0.imprint","INTERSECT",VERTEX,{"derivedFrom":[subQ1,subQ3]});Q26=makeQuery(id+"F0.imprint","IMPRINT",FACE,{"disambiguationData":[TD([[makeQuery(id+"F0.imprint","IMPRINT",EDGE,{"disambiguationData":[TD([[subQ4,1.0]])],"derivedFrom":subQ1}),-1.0]])]});}
            var Q27;
            {var subQ0=sQuery(id+"F0.wireOp",EDGE,"E48");var subQ3=sQuery(id+"F0.wireOp",EDGE,"E46");var subQ4=makeQuery(id+"F0.imprint","INTERSECT",VERTEX,{"derivedFrom":[subQ3,subQ0]});Q27=makeQuery(id+"F0.imprint","IMPRINT",FACE,{"disambiguationData":[TD([[makeQuery(id+"F0.imprint","IMPRINT",EDGE,{"disambiguationData":[TD([[subQ4,-1.0]])],"derivedFrom":subQ3}),-1.0]])]});}
            var Q28;
            {var subQ0=sQuery(id+"F0.wireOp",EDGE,"E47");var subQ1=sQuery(id+"F0.wireOp",EDGE,"E46");var subQ2=makeQuery(id+"F0.imprint","INTERSECT",VERTEX,{"derivedFrom":[subQ1,subQ0]});Q28=makeQuery(id+"F0.imprint","IMPRINT",FACE,{"disambiguationData":[TD([[makeQuery(id+"F0.imprint","IMPRINT",EDGE,{"disambiguationData":[TD([[subQ2,-1.0]])],"derivedFrom":subQ1}),1.0]])]});}
            var Q29;
            {var subQ0=sQuery(id+"F0.wireOp",EDGE,"E42");var subQ1=sQuery(id+"F0.wireOp",EDGE,"E4.bottom");var subQ2=makeQuery(id+"F0.imprint","INTERSECT",VERTEX,{"derivedFrom":[subQ1,subQ0]});Q29=makeQuery(id+"F0.imprint","IMPRINT",FACE,{"disambiguationData":[TD([[makeQuery(id+"F0.imprint","IMPRINT",EDGE,{"disambiguationData":[TD([[subQ2,1.0]])],"derivedFrom":subQ1}),1.0]])]});}
            var Q30;
            {var subQ0=sQuery(id+"F0.wireOp",EDGE,"E42");var subQ1=sQuery(id+"F0.wireOp",EDGE,"E4.bottom");var subQ2=makeQuery(id+"F0.imprint","INTERSECT",VERTEX,{"derivedFrom":[subQ1,subQ0]});Q30=makeQuery(id+"F0.imprint","IMPRINT",FACE,{"disambiguationData":[TD([[makeQuery(id+"F0.imprint","IMPRINT",EDGE,{"disambiguationData":[TD([[subQ2,-1.0]])],"derivedFrom":subQ1}),1.0]])]});}
            var Q31;
            {var subQ1=sQuery(id+"F0.wireOp",EDGE,"E44.9");var subQ3=sQuery(id+"F0.wireOp",EDGE,"E61");var subQ4=makeQuery(id+"F0.imprint","INTERSECT",VERTEX,{"derivedFrom":[subQ1,subQ3]});Q31=makeQuery(id+"F0.imprint","IMPRINT",FACE,{"disambiguationData":[TD([[makeQuery(id+"F0.imprint","IMPRINT",EDGE,{"disambiguationData":[TD([[subQ4,-1.0]])],"derivedFrom":subQ1}),1.0]])]});}
            var Q32;
            {var subQ0=sQuery(id+"F0.wireOp",EDGE,"E55");var subQ1=sQuery(id+"F0.wireOp",EDGE,"E47");var subQ2=makeQuery(id+"F0.imprint","INTERSECT",VERTEX,{"derivedFrom":[subQ1,subQ0]});Q32=makeQuery(id+"F0.imprint","IMPRINT",FACE,{"disambiguationData":[TD([[makeQuery(id+"F0.imprint","IMPRINT",EDGE,{"disambiguationData":[TD([[subQ2,-1.0]])],"derivedFrom":subQ1}),1.0]])]});}
            var Q33;
            {var subQ0=sQuery(id+"F0.wireOp",EDGE,"E50");var subQ5=sQuery(id+"F0.wireOp",EDGE,"E46");var subQ6=makeQuery(id+"F0.imprint","INTERSECT",VERTEX,{"derivedFrom":[subQ5,subQ0]});Q33=makeQuery(id+"F0.imprint","IMPRINT",FACE,{"disambiguationData":[TD([[makeQuery(id+"F0.imprint","IMPRINT",EDGE,{"disambiguationData":[TD([[subQ6,-1.0]])],"derivedFrom":subQ5}),-1.0]])]});}
            var Q34;
            {var subQ0=sQuery(id+"F0.wireOp",EDGE,"E50");var subQ1=sQuery(id+"F0.wireOp",EDGE,"E46");var subQ2=makeQuery(id+"F0.imprint","INTERSECT",VERTEX,{"derivedFrom":[subQ1,subQ0]});Q34=makeQuery(id+"F0.imprint","IMPRINT",FACE,{"disambiguationData":[TD([[makeQuery(id+"F0.imprint","IMPRINT",EDGE,{"disambiguationData":[TD([[subQ2,-1.0]])],"derivedFrom":subQ1}),1.0]])]});}
            var Q35;
            {var subQ0=sQuery(id+"F0.wireOp",EDGE,"E55");var subQ1=sQuery(id+"F0.wireOp",EDGE,"E50");var subQ2=makeQuery(id+"F0.imprint","INTERSECT",VERTEX,{"derivedFrom":[subQ1,subQ0]});Q35=makeQuery(id+"F0.imprint","IMPRINT",FACE,{"disambiguationData":[TD([[makeQuery(id+"F0.imprint","IMPRINT",EDGE,{"disambiguationData":[TD([[subQ2,-1.0]])],"derivedFrom":subQ1}),1.0]])]});}
            var Q36;
            {var subQ3=sQuery(id+"F0.wireOp",EDGE,"E61");var subQ5=sQuery(id+"F0.wireOp",EDGE,"E46");var subQ6=makeQuery(id+"F0.imprint","INTERSECT",VERTEX,{"disambiguationData":[OD(1.0)],"derivedFrom":[subQ5,subQ3]});Q36=makeQuery(id+"F0.imprint","IMPRINT",FACE,{"disambiguationData":[TD([[makeQuery(id+"F0.imprint","IMPRINT",EDGE,{"disambiguationData":[TD([[subQ6,-1.0]])],"derivedFrom":subQ5}),-1.0]])]});}
            var Q37;
            {var subQ1=sQuery(id+"F0.wireOp",EDGE,"E44.14");var subQ3=sQuery(id+"F0.wireOp",EDGE,"E60.bottom");var subQ4=makeQuery(id+"F0.imprint","INTERSECT",VERTEX,{"derivedFrom":[subQ1,subQ3]});Q37=makeQuery(id+"F0.imprint","IMPRINT",FACE,{"disambiguationData":[TD([[makeQuery(id+"F0.imprint","IMPRINT",EDGE,{"disambiguationData":[TD([[subQ4,-1.0]])],"derivedFrom":subQ1}),1.0]])]});}
            var Q38;
            {var subQ0=sQuery(id+"F0.wireOp",EDGE,"E48");var subQ5=sQuery(id+"F0.wireOp",EDGE,"E46");var subQ6=makeQuery(id+"F0.imprint","INTERSECT",VERTEX,{"derivedFrom":[subQ5,subQ0]});Q38=makeQuery(id+"F0.imprint","IMPRINT",FACE,{"disambiguationData":[TD([[makeQuery(id+"F0.imprint","IMPRINT",EDGE,{"disambiguationData":[TD([[subQ6,1.0]])],"derivedFrom":subQ5}),-1.0]])]});}
            var Q39;
            {var subQ1=sQuery(id+"F0.wireOp",EDGE,"E46");var subQ5=sQuery(id+"F0.wireOp",EDGE,"E48");var subQ6=makeQuery(id+"F0.imprint","INTERSECT",VERTEX,{"derivedFrom":[subQ1,subQ5]});Q39=makeQuery(id+"F0.imprint","IMPRINT",FACE,{"disambiguationData":[TD([[makeQuery(id+"F0.imprint","IMPRINT",EDGE,{"disambiguationData":[TD([[subQ6,1.0]])],"derivedFrom":subQ1}),1.0]])]});}
            var Q40;
            {var subQ0=sQuery(id+"F0.wireOp",EDGE,"E55");var subQ1=sQuery(id+"F0.wireOp",EDGE,"E48");var subQ2=makeQuery(id+"F0.imprint","INTERSECT",VERTEX,{"derivedFrom":[subQ1,subQ0]});Q40=makeQuery(id+"F0.imprint","IMPRINT",FACE,{"disambiguationData":[TD([[makeQuery(id+"F0.imprint","IMPRINT",EDGE,{"disambiguationData":[TD([[subQ2,-1.0]])],"derivedFrom":subQ1}),-1.0]])]});}
            var Q41;
            {var subQ3=sQuery(id+"F0.wireOp",EDGE,"E56");var subQ5=sQuery(id+"F0.wireOp",EDGE,"E32");var subQ6=makeQuery(id+"F0.imprint","INTERSECT",VERTEX,{"disambiguationData":[OD(0.0)],"derivedFrom":[subQ5,subQ3]});Q41=makeQuery(id+"F0.imprint","IMPRINT",FACE,{"disambiguationData":[TD([[makeQuery(id+"F0.imprint","IMPRINT",EDGE,{"disambiguationData":[TD([[subQ6,-1.0]])],"derivedFrom":subQ5}),1.0]])]});}
            var Q42;
            {var subQ0=sQuery(id+"F0.wireOp",EDGE,"E46");var subQ1=sQuery(id+"F0.wireOp",EDGE,"E32");var subQ2=makeQuery(id+"F0.imprint","INTERSECT",VERTEX,{"disambiguationData":[OD(0.0)],"derivedFrom":[subQ1,subQ0]});Q42=makeQuery(id+"F0.imprint","IMPRINT",FACE,{"disambiguationData":[TD([[makeQuery(id+"F0.imprint","IMPRINT",EDGE,{"disambiguationData":[TD([[subQ2,-1.0]])],"derivedFrom":subQ1}),1.0]])]});}
            var Q43;
            {var subQ0=sQuery(id+"F0.wireOp",EDGE,"E56");var subQ1=sQuery(id+"F0.wireOp",EDGE,"E32");var subQ2=makeQuery(id+"F0.imprint","INTERSECT",VERTEX,{"disambiguationData":[OD(1.0)],"derivedFrom":[subQ1,subQ0]});Q43=makeQuery(id+"F0.imprint","IMPRINT",FACE,{"disambiguationData":[TD([[makeQuery(id+"F0.imprint","IMPRINT",EDGE,{"disambiguationData":[TD([[subQ2,-1.0]])],"derivedFrom":subQ1}),1.0]])]});}
            var Q44;
            {var subQ0=sQuery(id+"F0.wireOp",EDGE,"E54");var subQ5=sQuery(id+"F0.wireOp",EDGE,"E46");var subQ6=makeQuery(id+"F0.imprint","INTERSECT",VERTEX,{"derivedFrom":[subQ5,subQ0]});Q44=makeQuery(id+"F0.imprint","IMPRINT",FACE,{"disambiguationData":[TD([[makeQuery(id+"F0.imprint","IMPRINT",EDGE,{"disambiguationData":[TD([[subQ6,-1.0]])],"derivedFrom":subQ5}),-1.0]])]});}
            extrude(context, id + "F1", {"entities" : qUnion([Q0, Q1, Q2, Q3, Q4, Q5, Q6, Q7, Q8, Q9, Q10, Q11, Q12, Q13, Q14, Q15, Q16, Q17, Q18, Q19, Q20, Q21, Q22, Q23, Q24, Q25, Q26, Q27, Q28, Q29, Q30, Q31, Q32, Q33, Q34, Q35, Q36, Q37, Q38, Q39, Q40, Q41, Q42, Q43, Q44]), "depth" : 4.7 * mm, "offsetDistance" : 25 * mm});
        }
        {
            var Q0;
            Q0=makeQuery(id+"F1.opExtrude","SWEPT_EDGE",EDGE,{"disambiguationData":[OSD([sQuery(id+"F0.wireOp",EDGE,"E32"),sQuery(id+"F0.wireOp",EDGE,"E53")])]});
            var Q1;
            Q1=makeQuery(id+"F1.opExtrude","SWEPT_EDGE",EDGE,{"disambiguationData":[OSD([sQuery(id+"F0.wireOp",EDGE,"E32"),sQuery(id+"F0.wireOp",EDGE,"E51")])]});
            fillet(context, id + "F2", {"entities" : qUnion([Q0, Q1]), "radius" : 5 * mm, "tangentPropagation" : true, "allowEdgeOverflow" : false});
        }
        {
            var Q0;
            {var subQ1=sQuery(id+"F0.wireOp",EDGE,"CWTrbjSd-p9ir-Zju1-9z6i-MnSNEF0wIDjJ");var subQ3=sQuery(id+"F0.wireOp",EDGE,"E44.9");var subQ4=makeQuery(id+"F0.imprint","INTERSECT",VERTEX,{"derivedFrom":[subQ1,subQ3]});Q0=makeQuery(id+"F0.imprint","IMPRINT",FACE,{"disambiguationData":[TD([[makeQuery(id+"F0.imprint","IMPRINT",EDGE,{"disambiguationData":[TD([[subQ4,1.0]])],"derivedFrom":subQ1}),1.0]])]});}
            var Q1;
            {var subQ3=sQuery(id+"F0.wireOp",EDGE,"E46");var subQ5=sQuery(id+"F0.wireOp",EDGE,"E49");var subQ6=makeQuery(id+"F0.imprint","INTERSECT",VERTEX,{"derivedFrom":[subQ3,subQ5]});Q1=makeQuery(id+"F0.imprint","IMPRINT",FACE,{"disambiguationData":[TD([[makeQuery(id+"F0.imprint","IMPRINT",EDGE,{"disambiguationData":[TD([[subQ6,-1.0]])],"derivedFrom":subQ3}),-1.0]])]});}
            var Q2;
            {var subQ0=sQuery(id+"F0.wireOp",EDGE,"E60.bottom");var subQ1=sQuery(id+"F0.wireOp",EDGE,"E46");var subQ2=makeQuery(id+"F0.imprint","INTERSECT",VERTEX,{"disambiguationData":[OD(1.0)],"derivedFrom":[subQ1,subQ0]});Q2=makeQuery(id+"F0.imprint","IMPRINT",FACE,{"disambiguationData":[TD([[makeQuery(id+"F0.imprint","IMPRINT",EDGE,{"disambiguationData":[TD([[subQ2,-1.0]])],"derivedFrom":subQ1}),-1.0]])]});}
            var Q3;
            {var subQ0=sQuery(id+"F0.wireOp",EDGE,"E47");var subQ1=sQuery(id+"F0.wireOp",EDGE,"E46");var subQ2=makeQuery(id+"F0.imprint","INTERSECT",VERTEX,{"derivedFrom":[subQ1,subQ0]});Q3=makeQuery(id+"F0.imprint","IMPRINT",FACE,{"disambiguationData":[TD([[makeQuery(id+"F0.imprint","IMPRINT",EDGE,{"disambiguationData":[TD([[subQ2,-1.0]])],"derivedFrom":subQ1}),1.0]])]});}
            var Q4;
            {var subQ1=sQuery(id+"F0.wireOp",EDGE,"CWTrbjSd-p9ir-Zju1-9z6i-MnSNEF0wIDjJ");var subQ8=makeQuery(id+"F0.imprint","IMPRINT",VERTEX,{"derivedFrom":subQ1});Q4=makeQuery(id+"F0.imprint","IMPRINT",FACE,{"disambiguationData":[TD([[makeQuery(id+"F0.imprint","IMPRINT",EDGE,{"disambiguationData":[TD([[subQ8,1.0]])],"derivedFrom":subQ1}),1.0]])]});}
            var Q5;
            {var subQ1=sQuery(id+"F0.wireOp",EDGE,"E46");var subQ5=sQuery(id+"F0.wireOp",EDGE,"CWTrbjSd-p9ir-Zju1-9z6i-MnSNEF0wIDjJ");var subQ9=makeQuery(id+"F0.imprint","INTERSECT",VERTEX,{"disambiguationData":[OD(0.0)],"derivedFrom":[subQ5,subQ1]});Q5=makeQuery(id+"F0.imprint","IMPRINT",FACE,{"disambiguationData":[TD([[makeQuery(id+"F0.imprint","IMPRINT",EDGE,{"disambiguationData":[TD([[subQ9,-1.0]])],"derivedFrom":subQ5}),1.0]])]});}
            var Q6;
            {var subQ3=sQuery(id+"F0.wireOp",EDGE,"E56");var subQ5=sQuery(id+"F0.wireOp",EDGE,"E36");var subQ10=makeQuery(id+"F0.imprint","INTERSECT",VERTEX,{"disambiguationData":[OD(0.0)],"derivedFrom":[subQ5,subQ3]});Q6=makeQuery(id+"F0.imprint","IMPRINT",FACE,{"disambiguationData":[TD([[makeQuery(id+"F0.imprint","IMPRINT",EDGE,{"disambiguationData":[TD([[subQ10,-1.0]])],"derivedFrom":subQ5}),-1.0]])]});}
            var Q7;
            {var subQ3=sQuery(id+"F0.wireOp",EDGE,"E56");var subQ8=sQuery(id+"F0.wireOp",EDGE,"E36");var subQ9=makeQuery(id+"F0.imprint","INTERSECT",VERTEX,{"disambiguationData":[OD(0.0)],"derivedFrom":[subQ8,subQ3]});Q7=makeQuery(id+"F0.imprint","IMPRINT",FACE,{"disambiguationData":[TD([[makeQuery(id+"F0.imprint","IMPRINT",EDGE,{"disambiguationData":[TD([[subQ9,1.0]])],"derivedFrom":subQ8}),-1.0]])]});}
            var Q8;
            {var subQ0=sQuery(id+"F0.wireOp",EDGE,"E47");var subQ1=sQuery(id+"F0.wireOp",EDGE,"E46");var subQ2=makeQuery(id+"F0.imprint","INTERSECT",VERTEX,{"derivedFrom":[subQ1,subQ0]});Q8=makeQuery(id+"F0.imprint","IMPRINT",FACE,{"disambiguationData":[TD([[makeQuery(id+"F0.imprint","IMPRINT",EDGE,{"disambiguationData":[TD([[subQ2,-1.0]])],"derivedFrom":subQ1}),-1.0]])]});}
            var Q9;
            {var subQ0=sQuery(id+"F0.wireOp",EDGE,"E48");var subQ3=sQuery(id+"F0.wireOp",EDGE,"E46");var subQ4=makeQuery(id+"F0.imprint","INTERSECT",VERTEX,{"derivedFrom":[subQ3,subQ0]});Q9=makeQuery(id+"F0.imprint","IMPRINT",FACE,{"disambiguationData":[TD([[makeQuery(id+"F0.imprint","IMPRINT",EDGE,{"disambiguationData":[TD([[subQ4,-1.0]])],"derivedFrom":subQ3}),-1.0]])]});}
            var Q10;
            {var subQ1=sQuery(id+"F0.wireOp",EDGE,"Fv1uCipX-vUk0-Yfkj-1D7Z-x97Jl5sTBQmt");var subQ3=sQuery(id+"F0.wireOp",EDGE,"E44.15");var subQ4=makeQuery(id+"F0.imprint","INTERSECT",VERTEX,{"derivedFrom":[subQ1,subQ3]});Q10=makeQuery(id+"F0.imprint","IMPRINT",FACE,{"disambiguationData":[TD([[makeQuery(id+"F0.imprint","IMPRINT",EDGE,{"disambiguationData":[TD([[subQ4,1.0]])],"derivedFrom":subQ1}),-1.0]])]});}
            var Q11;
            {var subQ0=sQuery(id+"F0.wireOp",EDGE,"E44.15");var subQ1=sQuery(id+"F0.wireOp",EDGE,"Fv1uCipX-vUk0-Yfkj-1D7Z-x97Jl5sTBQmt");var subQ2=makeQuery(id+"F0.imprint","INTERSECT",VERTEX,{"derivedFrom":[subQ1,subQ0]});Q11=makeQuery(id+"F0.imprint","IMPRINT",FACE,{"disambiguationData":[TD([[makeQuery(id+"F0.imprint","IMPRINT",EDGE,{"disambiguationData":[TD([[subQ2,-1.0]])],"derivedFrom":subQ1}),-1.0]])]});}
            var Q12;
            {var subQ1=sQuery(id+"F0.wireOp",EDGE,"E46");var subQ5=sQuery(id+"F0.wireOp",EDGE,"Fv1uCipX-vUk0-Yfkj-1D7Z-x97Jl5sTBQmt");var subQ9=makeQuery(id+"F0.imprint","INTERSECT",VERTEX,{"disambiguationData":[OD(0.0)],"derivedFrom":[subQ5,subQ1]});Q12=makeQuery(id+"F0.imprint","IMPRINT",FACE,{"disambiguationData":[TD([[makeQuery(id+"F0.imprint","IMPRINT",EDGE,{"disambiguationData":[TD([[subQ9,-1.0]])],"derivedFrom":subQ5}),-1.0]])]});}
            var Q13;
            {var subQ3=sQuery(id+"F0.wireOp",EDGE,"E56");var subQ8=sQuery(id+"F0.wireOp",EDGE,"E35");var subQ9=makeQuery(id+"F0.imprint","INTERSECT",VERTEX,{"disambiguationData":[OD(0.0)],"derivedFrom":[subQ8,subQ3]});Q13=makeQuery(id+"F0.imprint","IMPRINT",FACE,{"disambiguationData":[TD([[makeQuery(id+"F0.imprint","IMPRINT",EDGE,{"disambiguationData":[TD([[subQ9,-1.0]])],"derivedFrom":subQ8}),-1.0]])]});}
            var Q14;
            {var subQ5=sQuery(id+"F0.wireOp",EDGE,"E56");var subQ8=sQuery(id+"F0.wireOp",EDGE,"E35");var subQ9=makeQuery(id+"F0.imprint","INTERSECT",VERTEX,{"disambiguationData":[OD(0.0)],"derivedFrom":[subQ8,subQ5]});Q14=makeQuery(id+"F0.imprint","IMPRINT",FACE,{"disambiguationData":[TD([[makeQuery(id+"F0.imprint","IMPRINT",EDGE,{"disambiguationData":[TD([[subQ9,1.0]])],"derivedFrom":subQ8}),-1.0]])]});}
            var Q15;
            {var subQ0=sQuery(id+"F0.wireOp",EDGE,"E46");var subQ1=sQuery(id+"F0.wireOp",EDGE,"Fv1uCipX-vUk0-Yfkj-1D7Z-x97Jl5sTBQmt");var subQ2=makeQuery(id+"F0.imprint","INTERSECT",VERTEX,{"disambiguationData":[OD(1.0)],"derivedFrom":[subQ1,subQ0]});Q15=makeQuery(id+"F0.imprint","IMPRINT",FACE,{"disambiguationData":[TD([[makeQuery(id+"F0.imprint","IMPRINT",EDGE,{"disambiguationData":[TD([[subQ2,-1.0]])],"derivedFrom":subQ1}),-1.0]])]});}
            var Q16;
            {var subQ0=sQuery(id+"F0.wireOp",EDGE,"E53");var subQ1=sQuery(id+"F0.wireOp",EDGE,"E32");var subQ2=makeQuery(id+"F0.imprint","INTERSECT",VERTEX,{"derivedFrom":[subQ1,subQ0]});Q16=makeQuery(id+"F0.imprint","IMPRINT",FACE,{"disambiguationData":[TD([[makeQuery(id+"F0.imprint","IMPRINT",EDGE,{"disambiguationData":[TD([[subQ2,-1.0]])],"derivedFrom":subQ1}),1.0]])]});}
            var Q17;
            {var subQ3=sQuery(id+"F0.wireOp",EDGE,"E56");var subQ8=sQuery(id+"F0.wireOp",EDGE,"E38");var subQ9=makeQuery(id+"F0.imprint","INTERSECT",VERTEX,{"disambiguationData":[OD(0.0)],"derivedFrom":[subQ8,subQ3]});Q17=makeQuery(id+"F0.imprint","IMPRINT",FACE,{"disambiguationData":[TD([[makeQuery(id+"F0.imprint","IMPRINT",EDGE,{"disambiguationData":[TD([[subQ9,-1.0]])],"derivedFrom":subQ8}),-1.0]])]});}
            var Q18;
            {var subQ5=sQuery(id+"F0.wireOp",EDGE,"E56");var subQ8=sQuery(id+"F0.wireOp",EDGE,"E38");var subQ9=makeQuery(id+"F0.imprint","INTERSECT",VERTEX,{"disambiguationData":[OD(0.0)],"derivedFrom":[subQ8,subQ5]});Q18=makeQuery(id+"F0.imprint","IMPRINT",FACE,{"disambiguationData":[TD([[makeQuery(id+"F0.imprint","IMPRINT",EDGE,{"disambiguationData":[TD([[subQ9,1.0]])],"derivedFrom":subQ8}),-1.0]])]});}
            var Q19;
            {var subQ5=sQuery(id+"F0.wireOp",EDGE,"E34.filletArc");Q19=makeQuery(id+"F0.imprint","IMPRINT",FACE,{"disambiguationData":[TD([[makeQuery(id+"F0.imprint","IMPRINT",EDGE,{"derivedFrom":subQ5}),1.0]])]});}
            var Q20;
            {var subQ5=sQuery(id+"F0.wireOp",EDGE,"E56");var subQ7=sQuery(id+"F0.wireOp",EDGE,"E37");var subQ8=makeQuery(id+"F0.imprint","INTERSECT",VERTEX,{"disambiguationData":[OD(0.0)],"derivedFrom":[subQ7,subQ5]});Q20=makeQuery(id+"F0.imprint","IMPRINT",FACE,{"disambiguationData":[TD([[makeQuery(id+"F0.imprint","IMPRINT",EDGE,{"disambiguationData":[TD([[subQ8,1.0]])],"derivedFrom":subQ7}),-1.0]])]});}
            var Q21;
            {var subQ3=sQuery(id+"F0.wireOp",EDGE,"E56");var subQ8=sQuery(id+"F0.wireOp",EDGE,"E37");var subQ9=makeQuery(id+"F0.imprint","INTERSECT",VERTEX,{"disambiguationData":[OD(0.0)],"derivedFrom":[subQ8,subQ3]});Q21=makeQuery(id+"F0.imprint","IMPRINT",FACE,{"disambiguationData":[TD([[makeQuery(id+"F0.imprint","IMPRINT",EDGE,{"disambiguationData":[TD([[subQ9,-1.0]])],"derivedFrom":subQ8}),-1.0]])]});}
            var Q22;
            {var subQ1=sQuery(id+"F0.wireOp",EDGE,"E44.6");var subQ3=sQuery(id+"F0.wireOp",EDGE,"E32");var subQ4=makeQuery(id+"F0.imprint","INTERSECT",VERTEX,{"derivedFrom":[subQ3,subQ1]});Q22=makeQuery(id+"F0.imprint","IMPRINT",FACE,{"disambiguationData":[TD([[makeQuery(id+"F0.imprint","IMPRINT",EDGE,{"disambiguationData":[TD([[subQ4,-1.0]])],"derivedFrom":subQ3}),1.0]])]});}
            var Q23;
            {var subQ5=sQuery(id+"F0.wireOp",EDGE,"E33.filletArc");Q23=makeQuery(id+"F0.imprint","IMPRINT",FACE,{"disambiguationData":[TD([[makeQuery(id+"F0.imprint","IMPRINT",EDGE,{"derivedFrom":subQ5}),1.0]])]});}
            var Q24;
            {var subQ0=sQuery(id+"F0.wireOp",EDGE,"E46");var subQ1=sQuery(id+"F0.wireOp",EDGE,"CWTrbjSd-p9ir-Zju1-9z6i-MnSNEF0wIDjJ");var subQ2=makeQuery(id+"F0.imprint","INTERSECT",VERTEX,{"disambiguationData":[OD(1.0)],"derivedFrom":[subQ1,subQ0]});Q24=makeQuery(id+"F0.imprint","IMPRINT",FACE,{"disambiguationData":[TD([[makeQuery(id+"F0.imprint","IMPRINT",EDGE,{"disambiguationData":[TD([[subQ2,-1.0]])],"derivedFrom":subQ1}),1.0]])]});}
            var Q25;
            {var subQ1=sQuery(id+"F0.wireOp",EDGE,"E44.9");var subQ3=sQuery(id+"F0.wireOp",EDGE,"E61");var subQ4=makeQuery(id+"F0.imprint","INTERSECT",VERTEX,{"derivedFrom":[subQ1,subQ3]});Q25=makeQuery(id+"F0.imprint","IMPRINT",FACE,{"disambiguationData":[TD([[makeQuery(id+"F0.imprint","IMPRINT",EDGE,{"disambiguationData":[TD([[subQ4,-1.0]])],"derivedFrom":subQ1}),1.0]])]});}
            var Q26;
            {var subQ0=sQuery(id+"F0.wireOp",EDGE,"E55");var subQ1=sQuery(id+"F0.wireOp",EDGE,"E47");var subQ2=makeQuery(id+"F0.imprint","INTERSECT",VERTEX,{"derivedFrom":[subQ1,subQ0]});Q26=makeQuery(id+"F0.imprint","IMPRINT",FACE,{"disambiguationData":[TD([[makeQuery(id+"F0.imprint","IMPRINT",EDGE,{"disambiguationData":[TD([[subQ2,-1.0]])],"derivedFrom":subQ1}),1.0]])]});}
            var Q27;
            {var subQ1=sQuery(id+"F0.wireOp",EDGE,"E44.14");var subQ3=sQuery(id+"F0.wireOp",EDGE,"E60.bottom");var subQ4=makeQuery(id+"F0.imprint","INTERSECT",VERTEX,{"derivedFrom":[subQ1,subQ3]});Q27=makeQuery(id+"F0.imprint","IMPRINT",FACE,{"disambiguationData":[TD([[makeQuery(id+"F0.imprint","IMPRINT",EDGE,{"disambiguationData":[TD([[subQ4,-1.0]])],"derivedFrom":subQ1}),1.0]])]});}
            var Q28;
            {var subQ0=sQuery(id+"F0.wireOp",EDGE,"E48");var subQ5=sQuery(id+"F0.wireOp",EDGE,"E46");var subQ6=makeQuery(id+"F0.imprint","INTERSECT",VERTEX,{"derivedFrom":[subQ5,subQ0]});Q28=makeQuery(id+"F0.imprint","IMPRINT",FACE,{"disambiguationData":[TD([[makeQuery(id+"F0.imprint","IMPRINT",EDGE,{"disambiguationData":[TD([[subQ6,1.0]])],"derivedFrom":subQ5}),-1.0]])]});}
            var Q29;
            {var subQ1=sQuery(id+"F0.wireOp",EDGE,"E46");var subQ5=sQuery(id+"F0.wireOp",EDGE,"E48");var subQ6=makeQuery(id+"F0.imprint","INTERSECT",VERTEX,{"derivedFrom":[subQ1,subQ5]});Q29=makeQuery(id+"F0.imprint","IMPRINT",FACE,{"disambiguationData":[TD([[makeQuery(id+"F0.imprint","IMPRINT",EDGE,{"disambiguationData":[TD([[subQ6,1.0]])],"derivedFrom":subQ1}),1.0]])]});}
            var Q30;
            {var subQ0=sQuery(id+"F0.wireOp",EDGE,"E55");var subQ1=sQuery(id+"F0.wireOp",EDGE,"E48");var subQ2=makeQuery(id+"F0.imprint","INTERSECT",VERTEX,{"derivedFrom":[subQ1,subQ0]});Q30=makeQuery(id+"F0.imprint","IMPRINT",FACE,{"disambiguationData":[TD([[makeQuery(id+"F0.imprint","IMPRINT",EDGE,{"disambiguationData":[TD([[subQ2,-1.0]])],"derivedFrom":subQ1}),-1.0]])]});}
            var Q31;
            {var subQ0=sQuery(id+"F0.wireOp",EDGE,"E54");var subQ5=sQuery(id+"F0.wireOp",EDGE,"E46");var subQ6=makeQuery(id+"F0.imprint","INTERSECT",VERTEX,{"derivedFrom":[subQ5,subQ0]});Q31=makeQuery(id+"F0.imprint","IMPRINT",FACE,{"disambiguationData":[TD([[makeQuery(id+"F0.imprint","IMPRINT",EDGE,{"disambiguationData":[TD([[subQ6,-1.0]])],"derivedFrom":subQ5}),-1.0]])]});}
            var Q32;
            {var subQ0=sQuery(id+"F0.wireOp",EDGE,"E56");var subQ1=sQuery(id+"F0.wireOp",EDGE,"E32");var subQ2=makeQuery(id+"F0.imprint","INTERSECT",VERTEX,{"disambiguationData":[OD(1.0)],"derivedFrom":[subQ1,subQ0]});Q32=makeQuery(id+"F0.imprint","IMPRINT",FACE,{"disambiguationData":[TD([[makeQuery(id+"F0.imprint","IMPRINT",EDGE,{"disambiguationData":[TD([[subQ2,-1.0]])],"derivedFrom":subQ1}),1.0]])]});}
            var Q33;
            {var subQ3=sQuery(id+"F0.wireOp",EDGE,"E56");var subQ5=sQuery(id+"F0.wireOp",EDGE,"E32");var subQ6=makeQuery(id+"F0.imprint","INTERSECT",VERTEX,{"disambiguationData":[OD(0.0)],"derivedFrom":[subQ5,subQ3]});Q33=makeQuery(id+"F0.imprint","IMPRINT",FACE,{"disambiguationData":[TD([[makeQuery(id+"F0.imprint","IMPRINT",EDGE,{"disambiguationData":[TD([[subQ6,-1.0]])],"derivedFrom":subQ5}),1.0]])]});}
            var Q34;
            {var subQ0=sQuery(id+"F0.wireOp",EDGE,"E46");var subQ1=sQuery(id+"F0.wireOp",EDGE,"E32");var subQ2=makeQuery(id+"F0.imprint","INTERSECT",VERTEX,{"disambiguationData":[OD(0.0)],"derivedFrom":[subQ1,subQ0]});Q34=makeQuery(id+"F0.imprint","IMPRINT",FACE,{"disambiguationData":[TD([[makeQuery(id+"F0.imprint","IMPRINT",EDGE,{"disambiguationData":[TD([[subQ2,-1.0]])],"derivedFrom":subQ1}),1.0]])]});}
            var Q35;
            {var subQ0=sQuery(id+"F0.wireOp",EDGE,"E55");var subQ1=sQuery(id+"F0.wireOp",EDGE,"E50");var subQ2=makeQuery(id+"F0.imprint","INTERSECT",VERTEX,{"derivedFrom":[subQ1,subQ0]});Q35=makeQuery(id+"F0.imprint","IMPRINT",FACE,{"disambiguationData":[TD([[makeQuery(id+"F0.imprint","IMPRINT",EDGE,{"disambiguationData":[TD([[subQ2,-1.0]])],"derivedFrom":subQ1}),1.0]])]});}
            var Q36;
            {var subQ0=sQuery(id+"F0.wireOp",EDGE,"E50");var subQ1=sQuery(id+"F0.wireOp",EDGE,"E46");var subQ2=makeQuery(id+"F0.imprint","INTERSECT",VERTEX,{"derivedFrom":[subQ1,subQ0]});Q36=makeQuery(id+"F0.imprint","IMPRINT",FACE,{"disambiguationData":[TD([[makeQuery(id+"F0.imprint","IMPRINT",EDGE,{"disambiguationData":[TD([[subQ2,-1.0]])],"derivedFrom":subQ1}),1.0]])]});}
            var Q37;
            {var subQ3=sQuery(id+"F0.wireOp",EDGE,"E61");var subQ5=sQuery(id+"F0.wireOp",EDGE,"E46");var subQ6=makeQuery(id+"F0.imprint","INTERSECT",VERTEX,{"disambiguationData":[OD(1.0)],"derivedFrom":[subQ5,subQ3]});Q37=makeQuery(id+"F0.imprint","IMPRINT",FACE,{"disambiguationData":[TD([[makeQuery(id+"F0.imprint","IMPRINT",EDGE,{"disambiguationData":[TD([[subQ6,-1.0]])],"derivedFrom":subQ5}),-1.0]])]});}
            var Q38;
            {var subQ0=sQuery(id+"F0.wireOp",EDGE,"E50");var subQ5=sQuery(id+"F0.wireOp",EDGE,"E46");var subQ6=makeQuery(id+"F0.imprint","INTERSECT",VERTEX,{"derivedFrom":[subQ5,subQ0]});Q38=makeQuery(id+"F0.imprint","IMPRINT",FACE,{"disambiguationData":[TD([[makeQuery(id+"F0.imprint","IMPRINT",EDGE,{"disambiguationData":[TD([[subQ6,-1.0]])],"derivedFrom":subQ5}),-1.0]])]});}
            extrude(context, id + "F3", {"entities" : qUnion([Q0, Q1, Q2, Q3, Q4, Q5, Q6, Q7, Q8, Q9, Q10, Q11, Q12, Q13, Q14, Q15, Q16, Q17, Q18, Q19, Q20, Q21, Q22, Q23, Q24, Q25, Q26, Q27, Q28, Q29, Q30, Q31, Q32, Q33, Q34, Q35, Q36, Q37, Q38]), "operationType" : NewBodyOperationType.REMOVE, "depth" : .7 * mm, "offsetDistance" : 25 * mm});
        }
    });
